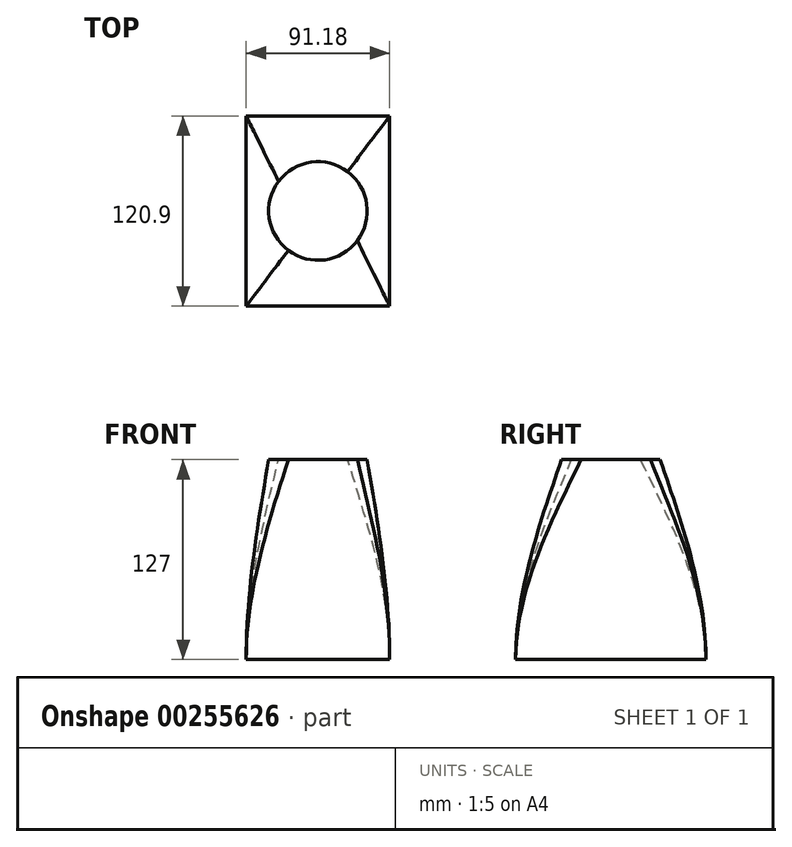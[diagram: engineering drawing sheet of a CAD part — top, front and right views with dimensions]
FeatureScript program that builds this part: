
annotation { "Feature Type Name" : "Feature", "Feature Type Description" : "" }
export const myFeature = defineFeature(function(context is Context, id is Id, definition is map)
    precondition{}
    {
        {
            var Q0;
            Q0=qCreatedBy(makeId("Top.planeOp"),FACE);
            var sketch = newSketch(context, id + "F0", { "sketchPlane" : qUnion([Q0])});
            skLineSegment(sketch, "E0.bottom", {"start": v(45.59, 60.45) * mm, "end": v(-45.59, 60.45) * mm});
            skLineSegment(sketch, "E0.top", {"start": v(45.59, -60.45) * mm, "end": v(-45.59, -60.45) * mm});
            skLineSegment(sketch, "E0.left", {"start": v(45.59, 60.45) * mm, "end": v(45.59, -60.45) * mm});
            skLineSegment(sketch, "E0.right", {"start": v(-45.59, 60.45) * mm, "end": v(-45.59, -60.45) * mm});
            skPoint(sketch, "E0.middle", {"position": v(0, 0) * mm});
            skSolve(sketch);
        }
        {
            var Q0;
            Q0=qCreatedBy(makeId("Top.planeOp"),FACE);
            cPlane(context, id + "F1", {"entities" : qUnion([Q0]), "cplaneType" : CPlaneType.OFFSET, "offset" : 127 * mm, "width" : 152.4 * mm, "height" : 152.4 * mm});
        }
        {
            var Q0;
            Q0=qCreatedBy(id+"F1.planeOp",FACE);
            var sketch = newSketch(context, id + "F2", { "sketchPlane" : qUnion([Q0])});
            skPoint(sketch, "E1.middle", {"position": v(0, 0) * mm});
            skCircle(sketch, "E2", {"center": v(0, 0) * mm, "radius": 31.3 * mm});
            skSolve(sketch);
        }
        {
            var Q0;
            Q0=makeQuery(id+"F0.imprint","IMPRINT",FACE,{"disambiguationData":[TD([[makeQuery(id+"F0.imprint","IMPRINT",EDGE,{"derivedFrom":sQuery(id+"F0.wireOp",EDGE,"E0.bottom")}),1.0]])]});
            var Q1;
            Q1=makeQuery(id+"F2.imprint","IMPRINT",FACE,{"disambiguationData":[TD([[makeQuery(id+"F2.imprint","IMPRINT",EDGE,{"derivedFrom":sQuery(id+"F2.wireOp",EDGE,"E2")}),1.0]])]});
            loft(context, id + "F3", {"startCondition" : LoftEndDerivativeType.NORMAL_TO_PROFILE, "startMagnitude" : 1, "sheetProfilesArray" : [{ "sheetProfileEntities" : qUnion([Q0]) }, { "sheetProfileEntities" : qUnion([Q1]) }]});
        }
    });
